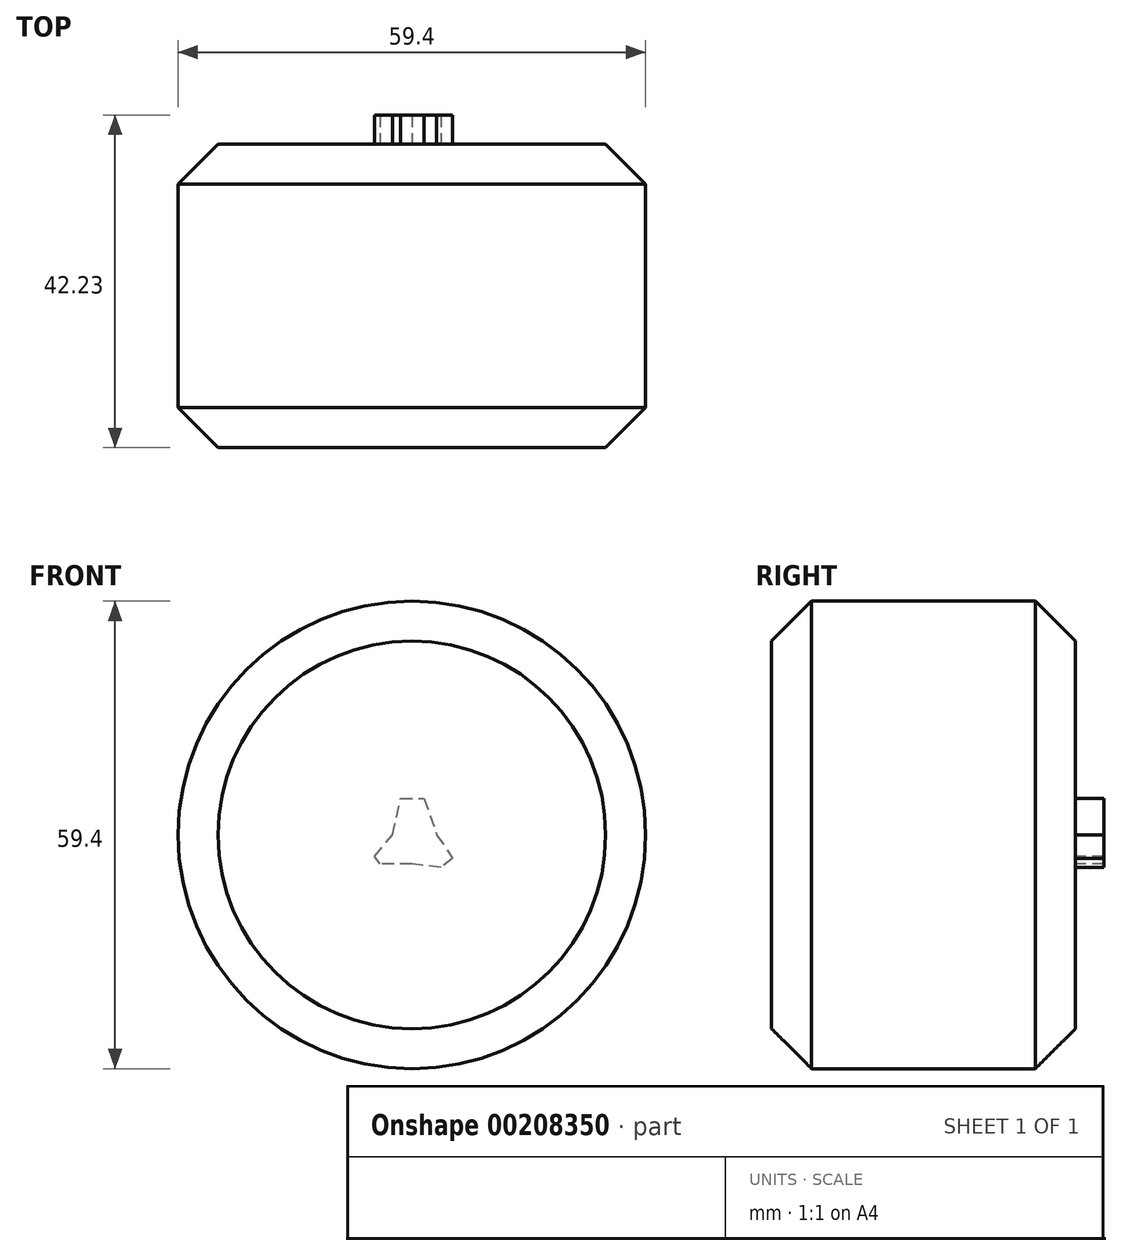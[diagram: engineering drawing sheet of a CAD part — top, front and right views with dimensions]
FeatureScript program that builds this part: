
annotation { "Feature Type Name" : "Feature", "Feature Type Description" : "" }
export const myFeature = defineFeature(function(context is Context, id is Id, definition is map)
    precondition{}
    {
        {
            var Q0;
            Q0=qCreatedBy(makeId("Front.planeOp"),FACE);
            var sketch = newSketch(context, id + "F0", { "sketchPlane" : qUnion([Q0])});
            skCircle(sketch, "E0", {"center": v(0, 0) * mm, "radius": 29.7 * mm});
            skSolve(sketch);
        }
        {
            var Q0;
            Q0 = qSketchRegion(id + "F0", true);
            extrude(context, id + "F2", {"entities" : qUnion([Q0]), "depth" : 38.58 * mm});
        }
        {
            var Q0;
            Q0=makeQuery(id+"F2.opExtrude","SWEPT_FACE",FACE,{"disambiguationData":[OSD([sQuery(id+"F0.wireOp",EDGE,"E0")])]});
            chamfer(context, id + "F1", {"entities" : qUnion([Q0]), "width" : 5.08 * mm, "tangentPropagation" : true});
        }
        {
            var Q0;
            Q0=makeQuery(id+"F2.opExtrude","CAP_FACE",FACE,{"disambiguationData":[OSD([sQuery(id+"F0.wireOp",EDGE,"E0")])],"isStart":false});
            var sketch = newSketch(context, id + "F3", { "sketchPlane" : qUnion([Q0])});
            skCircle(sketch, "E1", {"center": v(0, 0) * mm, "radius": 20.87 * mm});
            skCircle(sketch, "E2", {"center": v(0, 0) * mm, "radius": 17.6 * mm});
            skSolve(sketch);
        }
        {
            var Q0;
            Q0 = qSketchRegion(id + "F3", true);
            extrude(context, id + "F4", {"entities" : qUnion([Q0]), "operationType" : NewBodyOperationType.ADD, "oppositeDirection" : true, "depth" : 28.35 * mm});
        }
        {
            var Q0;
            Q0=makeQuery(id+"F4.boolean.opBoolean","SPLIT",FACE,{"disambiguationData":[TD([makeQuery(id+"F4.opExtrude","SWEPT_FACE",FACE,{"disambiguationData":[OSD([sQuery(id+"F3.wireOp",EDGE,"E2")])]})])],"derivedFrom":makeQuery(id+"F2.opExtrude","CAP_FACE",FACE,{"disambiguationData":[OSD([sQuery(id+"F0.wireOp",EDGE,"E0")])],"isStart":true})});
            var sketch = newSketch(context, id + "F5", { "sketchPlane" : qUnion([Q0])});
            skLineSegment(sketch, "E3", {"start": v(-2.23, 0) * mm, "end": v(2.48, 0) * mm});
            skLineSegment(sketch, "E4", {"start": v(2.48, 0) * mm, "end": v(1.43, 4.64) * mm});
            skLineSegment(sketch, "E5", {"start": v(1.43, 4.64) * mm, "end": v(-1.54, 4.64) * mm});
            skLineSegment(sketch, "E6", {"start": v(-1.54, 4.64) * mm, "end": v(-3.16, 0) * mm});
            skLineSegment(sketch, "E7", {"start": v(-3.16, 0) * mm, "end": v(-2.23, 0) * mm});
            skLineSegment(sketch, "E8", {"start": v(2.48, 0) * mm, "end": v(0, -3.71) * mm});
            skLineSegment(sketch, "E9", {"start": v(0, -3.71) * mm, "end": v(4.08, -3.71) * mm});
            skLineSegment(sketch, "E10", {"start": v(4.08, -3.71) * mm, "end": v(4.72, -2.77) * mm});
            skLineSegment(sketch, "E11", {"start": v(4.72, -2.77) * mm, "end": v(2.48, 0) * mm});
            skLineSegment(sketch, "E12", {"start": v(0, -3.71) * mm, "end": v(-3.16, 0) * mm});
            skLineSegment(sketch, "E13", {"start": v(-3.16, 0) * mm, "end": v(-5.19, -2.97) * mm});
            skLineSegment(sketch, "E14", {"start": v(-5.19, -2.97) * mm, "end": v(-3.67, -4.14) * mm});
            skLineSegment(sketch, "E15", {"start": v(-3.67, -4.14) * mm, "end": v(0, -3.71) * mm});
            skSolve(sketch);
        }
        {
            var Q0;
            Q0 = qSketchRegion(id + "F5", true);
            extrude(context, id + "F6", {"entities" : qUnion([Q0]), "operationType" : NewBodyOperationType.ADD, "depth" : 3.65 * mm});
        }
    });
